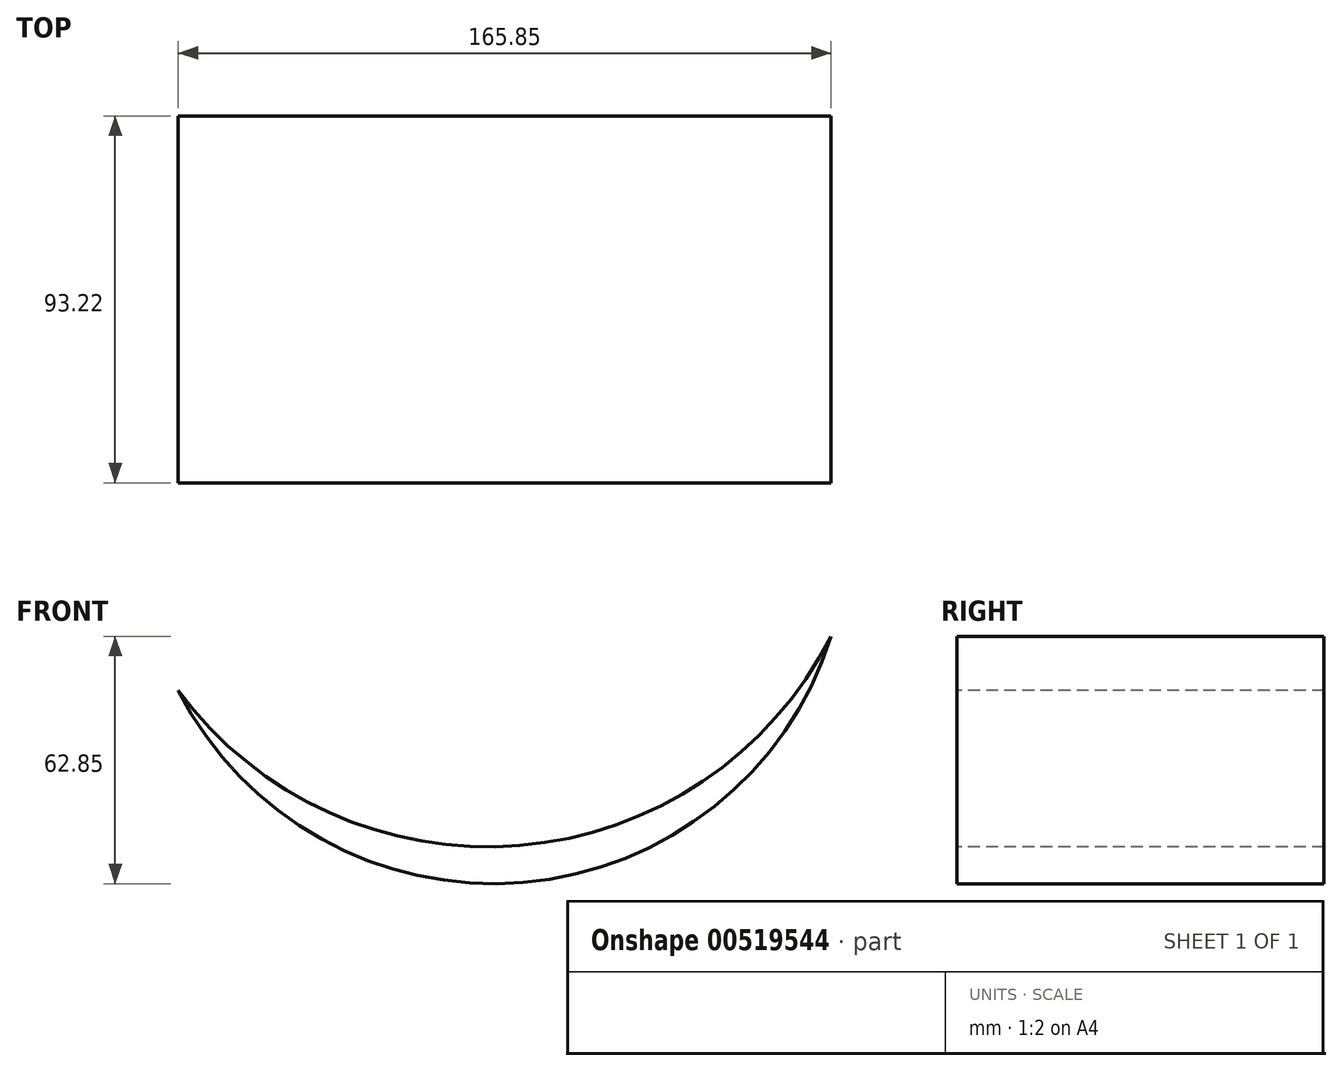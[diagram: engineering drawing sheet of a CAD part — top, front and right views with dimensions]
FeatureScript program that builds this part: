
annotation { "Feature Type Name" : "Feature", "Feature Type Description" : "" }
export const myFeature = defineFeature(function(context is Context, id is Id, definition is map)
    precondition{}
    {
        {
            var Q0;
            Q0=qCreatedBy(makeId("Front.planeOp"),FACE);
            var sketch = newSketch(context, id + "F0", { "sketchPlane" : qUnion([Q0])});
            skCircle(sketch, "E0", {"center": v(-39.34, 29) * mm, "radius": 89.92 * mm});
            skSolve(sketch);
        }
        {
            var Q0;
            Q0=makeQuery(id+"F0.imprint","IMPRINT",FACE,{"disambiguationData":[TD([[makeQuery(id+"F0.imprint","IMPRINT",EDGE,{"derivedFrom":sQuery(id+"F0.wireOp",EDGE,"E0")}),1.0]])]});
            extrude(context, id + "F1", {"entities" : qUnion([Q0]), "depth" : 93.22 * mm, "offsetDistance" : 25.4 * mm});
        }
        {
            var Q0;
            Q0=makeQuery(id+"F1.opExtrude","CAP_FACE",FACE,{"disambiguationData":[OSD([sQuery(id+"F0.wireOp",EDGE,"E0")])],"isStart":false});
            var sketch = newSketch(context, id + "F2", { "sketchPlane" : qUnion([Q0])});
            skCircle(sketch, "E1", {"center": v(-57.06, 31.06) * mm, "radius": 71.62 * mm});
            skSolve(sketch);
        }
        {
            var Q0;
            Q0=makeQuery(id+"F2.imprint","IMPRINT",FACE,{"disambiguationData":[TD([[makeQuery(id+"F2.imprint","IMPRINT",EDGE,{"derivedFrom":sQuery(id+"F2.wireOp",EDGE,"E1")}),1.0]])]});
            var sketch = newSketch(context, id + "F3", { "sketchPlane" : qUnion([Q0])});
            skCircle(sketch, "E2", {"center": v(-40.77, 46.22) * mm, "radius": 64.11 * mm});
            skSolve(sketch);
        }
        {
            var Q0;
            Q0=sQuery(id+"F3.wireOp",VERTEX,"E2.center");
            var Q1;
            Q1=makeQuery(id+"F1.opExtrude","SWEPT_BODY",BODY,{"disambiguationData":[OSD([sQuery(id+"F0.wireOp",EDGE,"E0")])]});
            hole(context, id + "F4", {"style" : HoleStyle.SIMPLE, "endStyle" : HoleEndStyle.THROUGH, "holeDiameter" : 195.58 * mm, "isTappedThrough" : true, "tappedDepth" : 12.7 * mm, "tapClearance" : 3, "locations" : qUnion([Q0]), "scope" : qUnion([Q1])});
        }
    });
